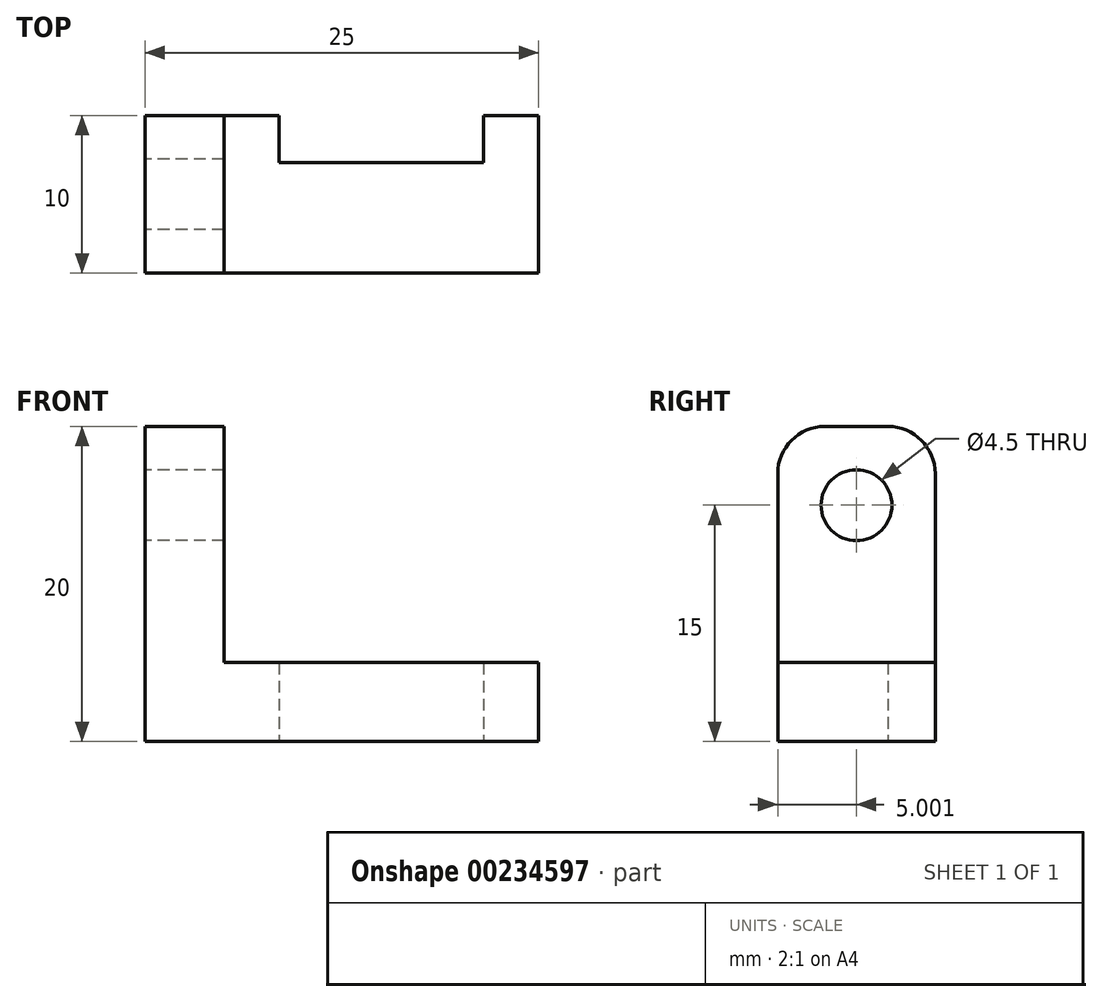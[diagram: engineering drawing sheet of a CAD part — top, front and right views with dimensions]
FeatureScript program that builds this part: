
annotation { "Feature Type Name" : "Feature", "Feature Type Description" : "" }
export const myFeature = defineFeature(function(context is Context, id is Id, definition is map)
    precondition{}
    {
        {
            var Q0;
            Q0=qCreatedBy(makeId("Top.planeOp"),FACE);
            var sketch = newSketch(context, id + "F0", { "sketchPlane" : qUnion([Q0])});
            skLineSegment(sketch, "E0.top", {"start": v(-15.62, -12.07) * mm, "end": v(9.38, -12.07) * mm});
            skLineSegment(sketch, "E0.left", {"start": v(-15.62, -2.07) * mm, "end": v(-15.62, -12.07) * mm});
            skLineSegment(sketch, "E0.right", {"start": v(9.38, -2.07) * mm, "end": v(9.38, -12.07) * mm});
            skLineSegment(sketch, "E1", {"start": v(-7.12, -2.07) * mm, "end": v(-7.12, -5.07) * mm});
            skLineSegment(sketch, "E2", {"start": v(-7.12, -5.07) * mm, "end": v(5.88, -5.07) * mm});
            skLineSegment(sketch, "E3", {"start": v(5.88, -5.07) * mm, "end": v(5.88, -2.07) * mm});
            skLineSegment(sketch, "E4.trimOffspring", {"start": v(5.88, -2.07) * mm, "end": v(9.38, -2.07) * mm});
            skLineSegment(sketch, "E5", {"start": v(-15.62, -2.07) * mm, "end": v(-7.12, -2.07) * mm});
            skSolve(sketch);
        }
        {
            var Q0;
            Q0 = qSketchRegion(id + "F0", true);
            var Q1;
            Q1=makeQuery(id+"F0.imprint","IMPRINT",FACE,{"disambiguationData":[TD([[makeQuery(id+"F0.imprint","IMPRINT",EDGE,{"derivedFrom":sQuery(id+"F0.wireOp",EDGE,"E0.top")}),1.0]])]});
            extrude(context, id + "F1", {"entities" : qUnion([Q0, Q1]), "depth" : 5 * mm});
        }
        {
            var Q0;
            Q0=makeQuery(id+"F1.opExtrude","CAP_FACE",FACE,{"disambiguationData":[OSD([sQuery(id+"F0.wireOp",EDGE,"E0.top"),sQuery(id+"F0.wireOp",EDGE,"E0.left"),sQuery(id+"F0.wireOp",EDGE,"E0.right"),sQuery(id+"F0.wireOp",EDGE,"E1"),sQuery(id+"F0.wireOp",EDGE,"E2"),sQuery(id+"F0.wireOp",EDGE,"E3"),sQuery(id+"F0.wireOp",EDGE,"E4.trimOffspring"),sQuery(id+"F0.wireOp",EDGE,"E5")])],"isStart":false});
            var sketch = newSketch(context, id + "F2", { "sketchPlane" : qUnion([Q0])});
            skLineSegment(sketch, "E6", {"start": v(-10.62, -2.07) * mm, "end": v(-10.62, -12.07) * mm});
            skSolve(sketch);
        }
        {
            var Q0;
            {var subQ0=sQuery(id+"F2.wireOp",EDGE,"E6");Q0=makeQuery(id+"F2.imprint","IMPRINT",FACE,{"disambiguationData":[TD([[makeQuery(id+"F2.imprint","IMPRINT",EDGE,{"derivedFrom":subQ0}),-1.0]])]});}
            extrude(context, id + "F3", {"entities" : qUnion([Q0]), "operationType" : NewBodyOperationType.ADD, "depth" : 15 * mm});
        }
        {
            var Q0;
            {var subQ0=sQuery(id+"F0.wireOp",EDGE,"E0.left");Q0=makeQuery(id+"F3.boolean.opBoolean","MERGE",FACE,{"derivedFrom":[makeQuery(id+"F1.opExtrude","SWEPT_FACE",FACE,{"disambiguationData":[OSD([subQ0])]}),makeQuery(id+"F3.opExtrude","SWEPT_FACE",FACE,{"disambiguationData":[OSD([subQ0])]})]});}
            var sketch = newSketch(context, id + "F4", { "sketchPlane" : qUnion([Q0])});
            skCircle(sketch, "E7", {"center": v(7.07, 15) * mm, "radius": 2.25 * mm});
            skSolve(sketch);
        }
        {
            var Q0;
            Q0=makeQuery(id+"F4.imprint","IMPRINT",FACE,{"disambiguationData":[TD([[makeQuery(id+"F4.imprint","IMPRINT",EDGE,{"derivedFrom":sQuery(id+"F4.wireOp",EDGE,"E7")}),1.0]])]});
            extrude(context, id + "F5", {"entities" : qUnion([Q0]), "operationType" : NewBodyOperationType.REMOVE, "oppositeDirection" : true, "depth" : 25 * mm});
        }
        {
            var Q0;
            Q0=makeQuery(id+"F3.opExtrude","CAP_EDGE",EDGE,{"disambiguationData":[OSD([sQuery(id+"F0.wireOp",EDGE,"E0.top")])],"isStart":false});
            var Q1;
            Q1=makeQuery(id+"F3.opExtrude","CAP_EDGE",EDGE,{"disambiguationData":[OSD([sQuery(id+"F0.wireOp",EDGE,"E5")])],"isStart":false});
            fillet(context, id + "F6", {"entities" : qUnion([Q0, Q1]), "radius" : 3 * mm, "tangentPropagation" : true, "allowEdgeOverflow" : false});
        }
    });
